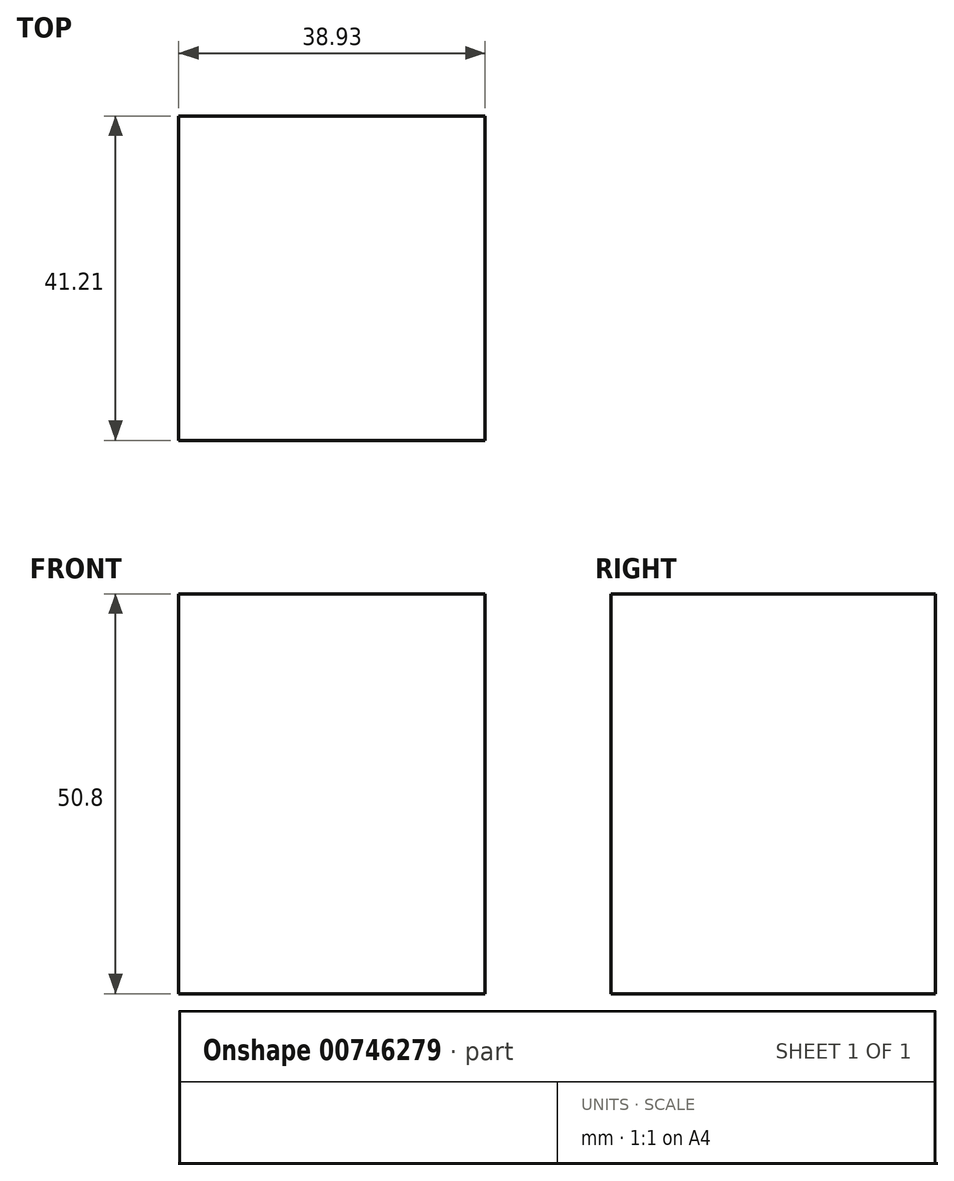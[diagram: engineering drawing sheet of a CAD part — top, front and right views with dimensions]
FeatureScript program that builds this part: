
annotation { "Feature Type Name" : "Feature", "Feature Type Description" : "" }
export const myFeature = defineFeature(function(context is Context, id is Id, definition is map)
    precondition{}
    {
        {
            var Q0;
            Q0=qCreatedBy(makeId("Top.planeOp"),FACE);
            var sketch = newSketch(context, id + "F0", { "sketchPlane" : qUnion([Q0])});
            skLineSegment(sketch, "E0.bottom", {"start": v(-20.54, 41.21) * mm, "end": v(18.4, 41.21) * mm});
            skLineSegment(sketch, "E0.top", {"start": v(-20.54, 0) * mm, "end": v(18.4, 0) * mm});
            skLineSegment(sketch, "E0.left", {"start": v(-20.54, 41.21) * mm, "end": v(-20.54, 0) * mm});
            skLineSegment(sketch, "E0.right", {"start": v(18.4, 41.21) * mm, "end": v(18.4, 0) * mm});
            skSolve(sketch);
        }
        {
            var Q0;
            Q0 = qSketchRegion(id + "F0", true);
            extrude(context, id + "F1", {"entities" : qUnion([Q0]), "depth" : 50.8 * mm, "offsetDistance" : 25.4 * mm});
        }
    });
